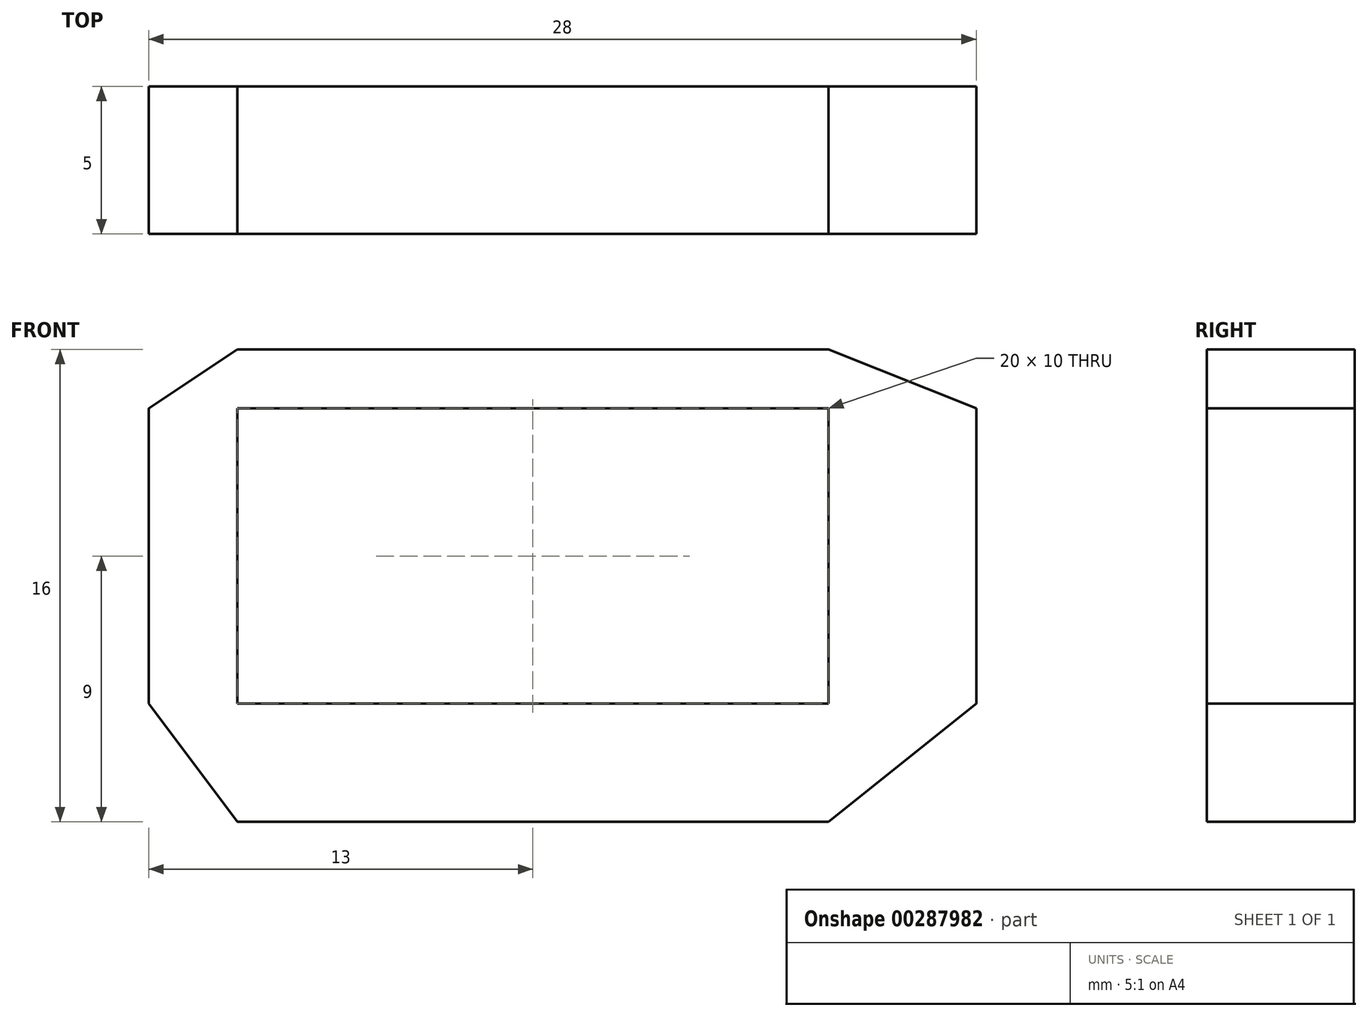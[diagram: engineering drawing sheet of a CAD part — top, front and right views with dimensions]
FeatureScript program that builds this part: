
annotation { "Feature Type Name" : "Feature", "Feature Type Description" : "" }
export const myFeature = defineFeature(function(context is Context, id is Id, definition is map)
    precondition{}
    {
        {
            var Q0;
            Q0=qCreatedBy(makeId("Front.planeOp"),FACE);
            var sketch = newSketch(context, id + "F0", { "sketchPlane" : qUnion([Q0])});
            skLineSegment(sketch, "E0", {"start": v(0, 0) * mm, "end": v(0, 10) * mm});
            skLineSegment(sketch, "E1", {"start": v(0, 10) * mm, "end": v(-20, 10) * mm});
            skLineSegment(sketch, "E2", {"start": v(-20, 10) * mm, "end": v(-20, 0) * mm});
            skLineSegment(sketch, "E3", {"start": v(-20, 0) * mm, "end": v(0, 0) * mm});
            skLineSegment(sketch, "E4.0", {"start": v(0, 12) * mm, "end": v(-20, 12) * mm});
            skLineSegment(sketch, "E5.0", {"start": v(-23, 10) * mm, "end": v(-23, 0) * mm});
            skLineSegment(sketch, "E6.MirrorCS", {"start": v(0, 0) * mm, "end": v(0, -10) * mm});
            skLineSegment(sketch, "E7.0", {"start": v(-20, -4) * mm, "end": v(0, -4) * mm});
            skLineSegment(sketch, "E8.0", {"start": v(5, 0) * mm, "end": v(5, 10) * mm});
            skLineSegment(sketch, "E9", {"start": v(-20, 12) * mm, "end": v(-23, 10) * mm});
            skLineSegment(sketch, "E10", {"start": v(-23, 0) * mm, "end": v(-20, -4) * mm});
            skLineSegment(sketch, "E11", {"start": v(0, -4) * mm, "end": v(5, 0) * mm});
            skLineSegment(sketch, "E12", {"start": v(5, 10) * mm, "end": v(0, 12) * mm});
            skSolve(sketch);
        }
        {
            var Q0;
            Q0=makeQuery(id+"F0.imprint","IMPRINT",FACE,{"disambiguationData":[TD([[makeQuery(id+"F0.imprint","IMPRINT",EDGE,{"derivedFrom":sQuery(id+"F0.wireOp",EDGE,"E0")}),-1.0]])]});
            extrude(context, id + "F1", {"entities" : qUnion([Q0]), "depth" : 5 * mm});
        }
    });
